# Revit family: Schienengleiter 45 M12
name_source: partatom
category: HLS-Bauteile
revit_build: Autodesk Revit 2017 (Build: 20190507_1515(x64)
units: mm (PartAtom-declared; Revit-internal decimal feet)

## family parameters
Arbeitsebenenbasiert = Ja
Beim Laden mit Abzugskörper schneiden = Nein
Bemaßung runder Anschluss = Durchmesser verwenden
Gemeinsam genutzt = Ja
Immer vertikal = Nein
Raumberechnungspunkt = Nein
Teiletyp = Normal

## types (1)
- Schienengleiter 45 M12
    Anschluss = 1 x M12
    Anzahl Anschlüsse = 1
    Artikelnummer = 077003201
    B1 = 36 mm  [stored 0.11811 ft]
    Breite = 35 mm  [stored 0.114829 ft]
    D0 = 17 mm  [stored 0.0557743 ft]
    EAN = 4250928417527
    Fabrikat = MEFA
    Gewicht = 0.13 kg
    Gewicht pro Bauteil = 0.13 kg
    Gewinde = M12
    H = 18 mm
    Kurztext1 = Schienengleiter axial 45
    Kurztext2 = Anschluss 1 x M12
    L = 72 mm  [stored 0.23622 ft]
    Länge = 90 mm  [stored 0.295276 ft]
    Mengeneinheit = St
    Vorgabe-Ansicht = 1219 mm
    max. zul. Last hängend = 2.00 kN
    vpe = 1 St

note: [stored X ft] marks values corroborated as IEEE doubles in the binary element streams (Revit-internal decimal feet)
